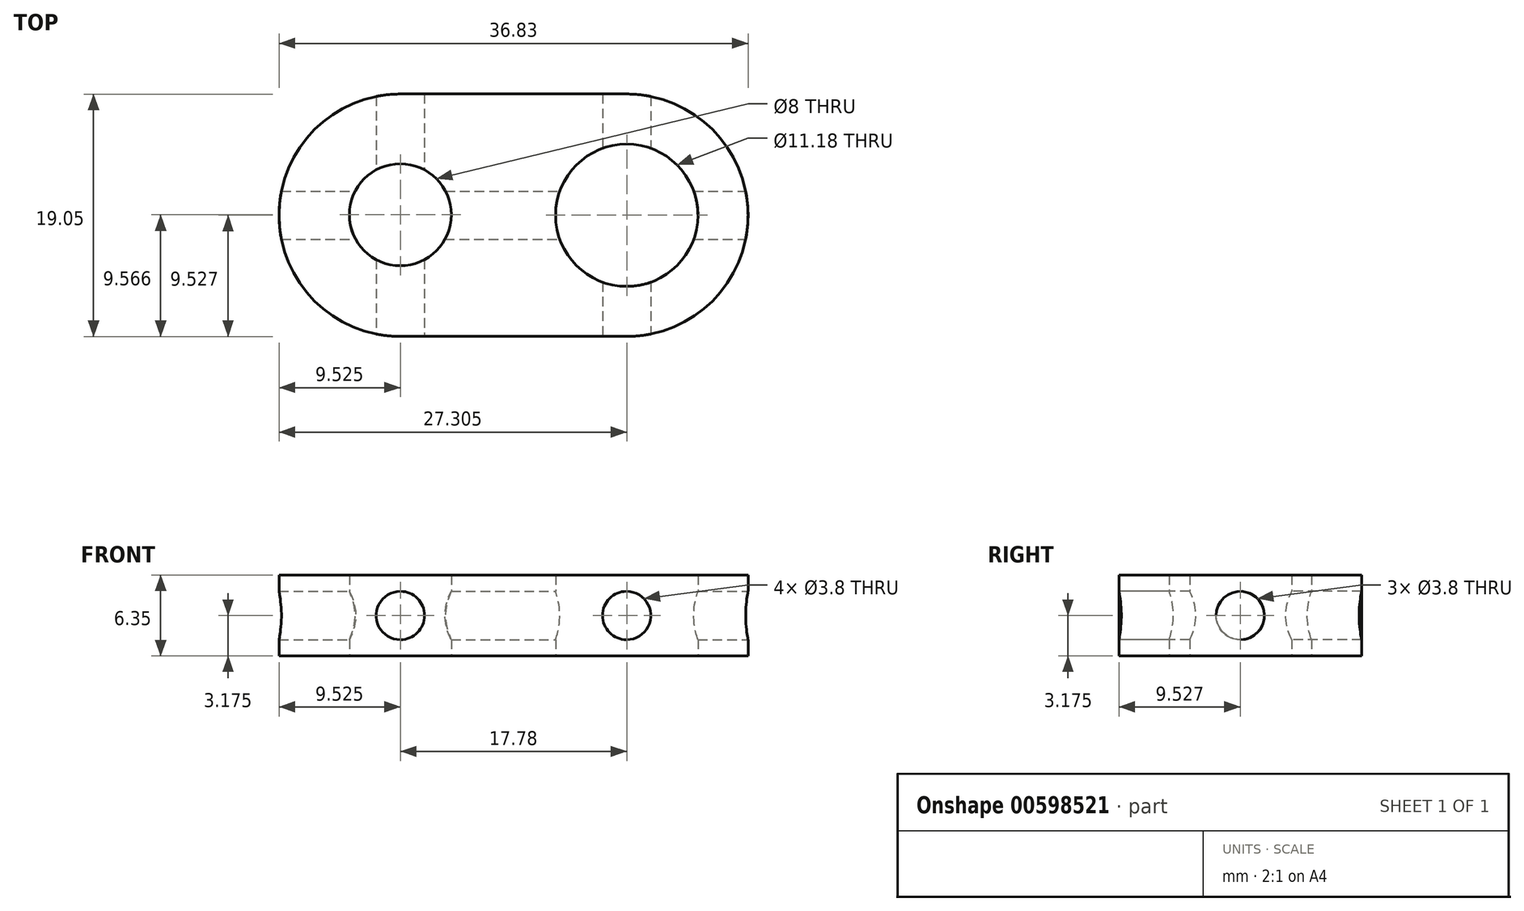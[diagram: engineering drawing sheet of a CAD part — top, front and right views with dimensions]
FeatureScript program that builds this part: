
annotation { "Feature Type Name" : "Feature", "Feature Type Description" : "" }
export const myFeature = defineFeature(function(context is Context, id is Id, definition is map)
    precondition{}
    {
        {
            var Q0;
            Q0=qCreatedBy(makeId("Top.planeOp"),FACE);
            var sketch = newSketch(context, id + "F0", { "sketchPlane" : qUnion([Q0])});
            skLineSegment(sketch, "E0.bottom", {"start": v(2.6, 46.44) * mm, "end": v(39.42, 46.44) * mm});
            skLineSegment(sketch, "E0.top", {"start": v(2.6, 27.4) * mm, "end": v(39.42, 27.4) * mm});
            skLineSegment(sketch, "E0.left", {"start": v(2.6, 46.44) * mm, "end": v(2.6, 27.4) * mm});
            skLineSegment(sketch, "E0.right", {"start": v(39.42, 46.44) * mm, "end": v(39.42, 27.4) * mm});
            skLineSegment(sketch, "E1", {"start": v(12.12, 48.85) * mm, "end": v(12.12, 25.06) * mm, "construction": true});
            skLineSegment(sketch, "E2", {"start": v(29.9, 48.92) * mm, "end": v(29.9, 20.99) * mm, "construction": true});
            skLineSegment(sketch, "E3", {"start": v(2.6, 36.92) * mm, "end": v(39.42, 36.92) * mm, "construction": true});
            skPoint(sketch, "E4", {"position": v(12.12, 36.96) * mm});
            skPoint(sketch, "E5", {"position": v(29.9, 36.92) * mm});
            skArc(sketch, "E6", {"start": v(12.12, 46.44) * mm, "mid": v(2.6, 36.92) * mm, "end": v(12.12, 27.4) * mm});
            skArc(sketch, "E7", {"start": v(29.9, 27.4) * mm, "mid": v(39.42, 36.92) * mm, "end": v(29.9, 46.44) * mm});
            skSolve(sketch);
        }
        {
            var Q0;
            {var subQ0=sQuery(id+"F0.wireOp",EDGE,"E6");var subQ1=sQuery(id+"F0.wireOp",EDGE,"E0.bottom");var subQ2=makeQuery(id+"F0.imprint","INTERSECT",VERTEX,{"derivedFrom":[subQ1,subQ0]});Q0=makeQuery(id+"F0.imprint","IMPRINT",FACE,{"disambiguationData":[TD([[makeQuery(id+"F0.imprint","IMPRINT",EDGE,{"disambiguationData":[TD([[subQ2,-1.0]])],"derivedFrom":subQ1}),-1.0]])]});}
            var Q1;
            {var subQ0=sQuery(id+"F0.wireOp",EDGE,"E0.left");var subQ1=sQuery(id+"F0.wireOp",EDGE,"E0.bottom");var subQ2=makeQuery(id+"F0.imprint","INTERSECT",VERTEX,{"derivedFrom":[subQ1,subQ0]});Q1=makeQuery(id+"F0.imprint","IMPRINT",FACE,{"disambiguationData":[TD([[makeQuery(id+"F0.imprint","IMPRINT",EDGE,{"disambiguationData":[TD([[subQ2,-1.0]])],"derivedFrom":subQ1}),-1.0]])]});}
            var Q2;
            {var subQ0=sQuery(id+"F0.wireOp",EDGE,"E0.left");var subQ1=sQuery(id+"F0.wireOp",EDGE,"E0.top");var subQ2=makeQuery(id+"F0.imprint","INTERSECT",VERTEX,{"derivedFrom":[subQ1,subQ0]});Q2=makeQuery(id+"F0.imprint","IMPRINT",FACE,{"disambiguationData":[TD([[makeQuery(id+"F0.imprint","IMPRINT",EDGE,{"disambiguationData":[TD([[subQ2,-1.0]])],"derivedFrom":subQ1}),1.0]])]});}
            var Q3;
            {var subQ0=sQuery(id+"F0.wireOp",EDGE,"E0.right");var subQ1=sQuery(id+"F0.wireOp",EDGE,"E0.top");var subQ2=makeQuery(id+"F0.imprint","INTERSECT",VERTEX,{"derivedFrom":[subQ1,subQ0]});Q3=makeQuery(id+"F0.imprint","IMPRINT",FACE,{"disambiguationData":[TD([[makeQuery(id+"F0.imprint","IMPRINT",EDGE,{"disambiguationData":[TD([[subQ2,1.0]])],"derivedFrom":subQ1}),1.0]])]});}
            var Q4;
            {var subQ0=sQuery(id+"F0.wireOp",EDGE,"E0.right");var subQ1=sQuery(id+"F0.wireOp",EDGE,"E0.bottom");var subQ2=makeQuery(id+"F0.imprint","INTERSECT",VERTEX,{"derivedFrom":[subQ1,subQ0]});Q4=makeQuery(id+"F0.imprint","IMPRINT",FACE,{"disambiguationData":[TD([[makeQuery(id+"F0.imprint","IMPRINT",EDGE,{"disambiguationData":[TD([[subQ2,1.0]])],"derivedFrom":subQ1}),-1.0]])]});}
            extrude(context, id + "F1", {"entities" : qUnion([Q0, Q1, Q2, Q3, Q4]), "oppositeDirection" : true, "depth" : 6.35 * mm, "offsetDistance" : 25.4 * mm});
        }
        {
            var Q0;
            Q0=makeQuery(id+"F1.opExtrude","SWEPT_FACE",FACE,{"disambiguationData":[OSD([sQuery(id+"F0.wireOp",EDGE,"E0.left")])]});
            var sketch = newSketch(context, id + "F2", { "sketchPlane" : qUnion([Q0])});
            skLineSegment(sketch, "E8", {"start": v(-46.44, -3.18) * mm, "end": v(-27.4, -3.18) * mm, "construction": true});
            skPoint(sketch, "E9", {"position": v(-36.92, -3.18) * mm});
            skSolve(sketch);
        }
        {
            var Q0;
            Q0=makeQuery(id+"F1.opExtrude","SWEPT_FACE",FACE,{"disambiguationData":[OSD([sQuery(id+"F0.wireOp",EDGE,"E0.bottom")])]});
            var sketch = newSketch(context, id + "F3", { "sketchPlane" : qUnion([Q0])});
            skLineSegment(sketch, "E10", {"start": v(-39.42, -3.18) * mm, "end": v(-2.6, -3.18) * mm, "construction": true});
            skPoint(sketch, "E11", {"position": v(-29.9, -3.18) * mm});
            skPoint(sketch, "E12", {"position": v(-12.12, -3.18) * mm});
            skSolve(sketch);
        }
        {
            var Q0;
            Q0=sQuery(id+"F2.wireOp",VERTEX,"E9");
            var Q1;
            Q1=sQuery(id+"F3.wireOp",VERTEX,"E12");
            var Q2;
            Q2=sQuery(id+"F3.wireOp",VERTEX,"E11");
            var Q3;
            Q3=makeQuery(id+"F1.opExtrude","SWEPT_BODY",BODY,{"disambiguationData":[OSD([sQuery(id+"F0.wireOp",EDGE,"E0.bottom"),sQuery(id+"F0.wireOp",EDGE,"E0.top"),sQuery(id+"F0.wireOp",EDGE,"E0.left"),sQuery(id+"F0.wireOp",EDGE,"E0.right")])]});
            hole(context, id + "F4", {"style" : HoleStyle.SIMPLE, "endStyle" : HoleEndStyle.THROUGH, "standardTappedOrClearance" : lookupTablePath({ "standard" : "ANSI", "engagement" : "75%", "pitch" : "24 tpi", "size" : "#10", "type" : "Tapped" }), "standardBlindInLast" : lookupTablePath({ "standard" : "ANSI", "engagement" : "75%", "pitch" : "24 tpi", "size" : "#10", "type" : "Tapped" }), "holeDiameter" : 3.8 * mm, "majorDiameter" : 4.83 * mm, "showTappedDepth" : true, "isTappedThrough" : true, "tappedDepth" : 6.35 * mm, "tapClearance" : 3, "locations" : qUnion([Q0, Q1, Q2]), "scope" : qUnion([Q3]), "startStyle" : HoleStartStyle.PART});
        }
        {
            var Q0;
            {var subQ0=sQuery(id+"F0.wireOp",EDGE,"E0.left");var subQ1=sQuery(id+"F0.wireOp",EDGE,"E0.bottom");var subQ2=makeQuery(id+"F0.imprint","INTERSECT",VERTEX,{"derivedFrom":[subQ1,subQ0]});Q0=makeQuery(id+"F0.imprint","IMPRINT",FACE,{"disambiguationData":[TD([[makeQuery(id+"F0.imprint","IMPRINT",EDGE,{"disambiguationData":[TD([[subQ2,-1.0]])],"derivedFrom":subQ1}),-1.0]])]});}
            var Q1;
            {var subQ0=sQuery(id+"F0.wireOp",EDGE,"E0.left");var subQ1=sQuery(id+"F0.wireOp",EDGE,"E0.top");var subQ2=makeQuery(id+"F0.imprint","INTERSECT",VERTEX,{"derivedFrom":[subQ1,subQ0]});Q1=makeQuery(id+"F0.imprint","IMPRINT",FACE,{"disambiguationData":[TD([[makeQuery(id+"F0.imprint","IMPRINT",EDGE,{"disambiguationData":[TD([[subQ2,-1.0]])],"derivedFrom":subQ1}),1.0]])]});}
            var Q2;
            {var subQ0=sQuery(id+"F0.wireOp",EDGE,"E0.right");var subQ1=sQuery(id+"F0.wireOp",EDGE,"E0.bottom");var subQ2=makeQuery(id+"F0.imprint","INTERSECT",VERTEX,{"derivedFrom":[subQ1,subQ0]});Q2=makeQuery(id+"F0.imprint","IMPRINT",FACE,{"disambiguationData":[TD([[makeQuery(id+"F0.imprint","IMPRINT",EDGE,{"disambiguationData":[TD([[subQ2,1.0]])],"derivedFrom":subQ1}),-1.0]])]});}
            var Q3;
            {var subQ0=sQuery(id+"F0.wireOp",EDGE,"E0.right");var subQ1=sQuery(id+"F0.wireOp",EDGE,"E0.top");var subQ2=makeQuery(id+"F0.imprint","INTERSECT",VERTEX,{"derivedFrom":[subQ1,subQ0]});Q3=makeQuery(id+"F0.imprint","IMPRINT",FACE,{"disambiguationData":[TD([[makeQuery(id+"F0.imprint","IMPRINT",EDGE,{"disambiguationData":[TD([[subQ2,1.0]])],"derivedFrom":subQ1}),1.0]])]});}
            extrude(context, id + "F5", {"entities" : qUnion([Q0, Q1, Q2, Q3]), "operationType" : NewBodyOperationType.REMOVE, "oppositeDirection" : true, "depth" : 25.4 * mm, "offsetDistance" : 25.4 * mm});
        }
        {
            var Q0;
            Q0=sQuery(id+"F0.wireOp",VERTEX,"E4");
            var Q1;
            Q1=makeQuery(id+"F1.opExtrude","SWEPT_BODY",BODY,{"disambiguationData":[OSD([sQuery(id+"F0.wireOp",EDGE,"E0.bottom"),sQuery(id+"F0.wireOp",EDGE,"E0.top"),sQuery(id+"F0.wireOp",EDGE,"E0.left"),sQuery(id+"F0.wireOp",EDGE,"E0.right")])]});
            hole(context, id + "F6", {"style" : HoleStyle.SIMPLE, "endStyle" : HoleEndStyle.THROUGH, "holeDiameter" : 8 * mm, "majorDiameter" : 4.83 * mm, "isTappedThrough" : true, "tappedDepth" : 6.35 * mm, "tapClearance" : 3, "locations" : qUnion([Q0]), "scope" : qUnion([Q1]), "startStyle" : HoleStartStyle.PART});
        }
        {
            var Q0;
            Q0=sQuery(id+"F0.wireOp",VERTEX,"E5");
            var Q1;
            Q1=makeQuery(id+"F1.opExtrude","SWEPT_BODY",BODY,{"disambiguationData":[OSD([sQuery(id+"F0.wireOp",EDGE,"E0.bottom"),sQuery(id+"F0.wireOp",EDGE,"E0.top"),sQuery(id+"F0.wireOp",EDGE,"E0.left"),sQuery(id+"F0.wireOp",EDGE,"E0.right")])]});
            hole(context, id + "F7", {"style" : HoleStyle.SIMPLE, "endStyle" : HoleEndStyle.THROUGH, "holeDiameter" : 11.18 * mm, "majorDiameter" : 6.35 * mm, "isTappedThrough" : true, "tappedDepth" : 6.35 * mm, "tapClearance" : 3, "locations" : qUnion([Q0]), "scope" : qUnion([Q1]), "startStyle" : HoleStartStyle.PART});
        }
    });
